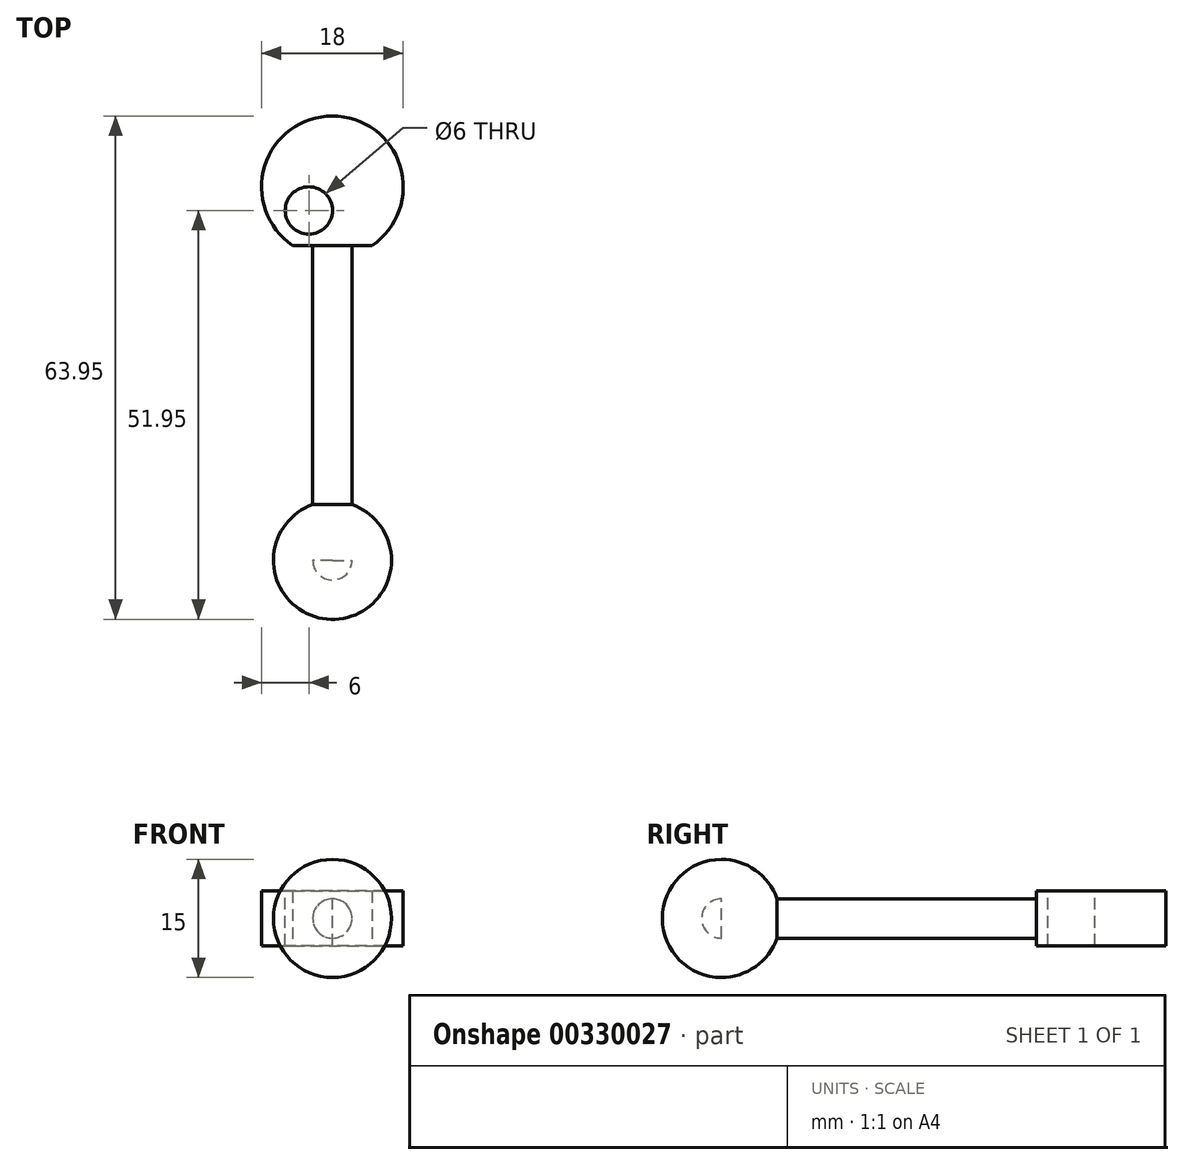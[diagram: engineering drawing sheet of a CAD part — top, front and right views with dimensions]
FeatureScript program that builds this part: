
annotation { "Feature Type Name" : "Feature", "Feature Type Description" : "" }
export const myFeature = defineFeature(function(context is Context, id is Id, definition is map)
    precondition{}
    {
        {
            var Q0;
            Q0=qCreatedBy(makeId("Top.planeOp"),FACE);
            var sketch = newSketch(context, id + "F0", { "sketchPlane" : qUnion([Q0])});
            skArc(sketch, "E0", {"start": v(5.05, -7.45) * mm, "mid": v(0, 9) * mm, "end": v(-5.05, -7.45) * mm});
            skLineSegment(sketch, "E1", {"start": v(-5.05, -7.45) * mm, "end": v(5.05, -7.45) * mm});
            skSolve(sketch);
        }
        {
            var Q0;
            Q0 = qSketchRegion(id + "F0", true);
            extrude(context, id + "F1", {"entities" : qUnion([Q0]), "depth" : 6.95 * mm});
        }
        {
            var Q0;
            Q0=makeQuery(id+"F1.opExtrude","SWEPT_FACE",FACE,{"disambiguationData":[OSD([sQuery(id+"F0.wireOp",EDGE,"E1")])]});
            var sketch = newSketch(context, id + "F2", { "sketchPlane" : qUnion([Q0])});
            skCircle(sketch, "E2", {"center": v(0, 3.48) * mm, "radius": 2.5 * mm});
            skPoint(sketch, "E2.centerSnap0", {"position": v(5.05, 3.48) * mm});
            skSolve(sketch);
        }
        {
            var Q0;
            Q0 = qSketchRegion(id + "F2", true);
            extrude(context, id + "F3", {"entities" : qUnion([Q0]), "operationType" : NewBodyOperationType.ADD, "depth" : 40 * mm});
        }
        {
            var Q0;
            Q0=makeQuery(id+"F3.opExtrude","CAP_FACE",FACE,{"disambiguationData":[OSD([sQuery(id+"F2.wireOp",EDGE,"E2")])],"isStart":false});
            var sketch = newSketch(context, id + "F4", { "sketchPlane" : qUnion([Q0])});
            skArc(sketch, "E3", {"start": v(0, -4.02) * mm, "mid": v(7.5, 3.47) * mm, "end": v(0, 10.97) * mm});
            skLineSegment(sketch, "E4", {"start": v(0, 10.97) * mm, "end": v(0, -4.02) * mm});
            skSolve(sketch);
        }
        {
            var Q0;
            {var subQ0=sQuery(id+"F4.wireOp",EDGE,"E3");Q0=makeQuery(id+"F4.imprint","IMPRINT",FACE,{"disambiguationData":[TD([[makeQuery(id+"F4.imprint","IMPRINT",EDGE,{"derivedFrom":subQ0}),1.0]])]});}
            var Q1;
            Q1=sQuery(id+"F4.wireOp",EDGE,"E4");
            revolve(context, id + "F5", {"operationType" : NewBodyOperationType.ADD, "entities" : qUnion([Q0]), "axis" : qUnion([Q1]), "revolveType" : RevolveType.FULL});
        }
        {
            var Q0;
            Q0=makeQuery(id+"F1.opExtrude","CAP_FACE",FACE,{"disambiguationData":[OSD([sQuery(id+"F0.wireOp",EDGE,"E0"),sQuery(id+"F0.wireOp",EDGE,"E1")])],"isStart":false});
            var sketch = newSketch(context, id + "F6", { "sketchPlane" : qUnion([Q0])});
            skCircle(sketch, "E5", {"center": v(-3, -3) * mm, "radius": 3 * mm});
            skLineSegment(sketch, "E6", {"start": v(0, 0) * mm, "end": v(-9, 0) * mm, "construction": true});
            skLineSegment(sketch, "E7", {"start": v(0, -0.35) * mm, "end": v(0, -7.45) * mm, "construction": true});
            skSolve(sketch);
        }
        {
            var Q0;
            Q0=makeQuery(id+"F6.imprint","IMPRINT",FACE,{"disambiguationData":[TD([[makeQuery(id+"F6.imprint","IMPRINT",EDGE,{"derivedFrom":sQuery(id+"F6.wireOp",EDGE,"E5")}),1.0]])]});
            extrude(context, id + "F7", {"entities" : qUnion([Q0]), "operationType" : NewBodyOperationType.REMOVE, "oppositeDirection" : true, "depth" : 10 * mm});
        }
    });
